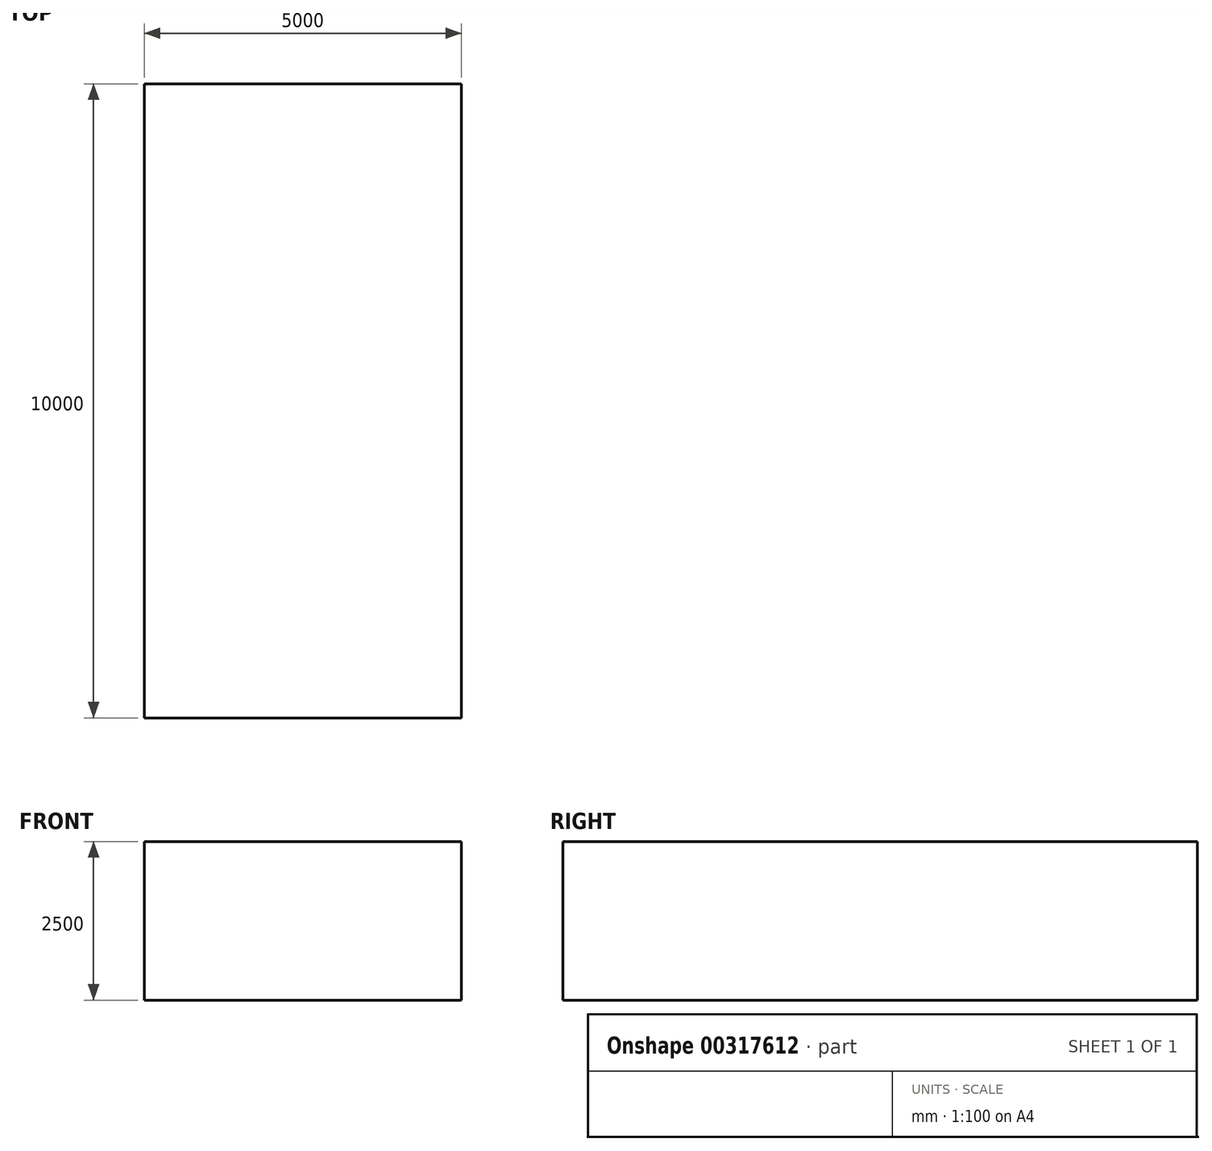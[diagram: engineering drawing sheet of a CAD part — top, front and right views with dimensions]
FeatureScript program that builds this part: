
annotation { "Feature Type Name" : "Feature", "Feature Type Description" : "" }
export const myFeature = defineFeature(function(context is Context, id is Id, definition is map)
    precondition{}
    {
        {
            var Q0;
            Q0=qCreatedBy(makeId("Front.planeOp"),FACE);
            var sketch = newSketch(context, id + "F0", { "sketchPlane" : qUnion([Q0])});
            skLineSegment(sketch, "E0.bottom", {"start": v(-2348.79, 1512.9) * mm, "end": v(2651.21, 1512.9) * mm});
            skLineSegment(sketch, "E0.top", {"start": v(-2348.79, -987.1) * mm, "end": v(2651.21, -987.1) * mm});
            skLineSegment(sketch, "E0.left", {"start": v(-2348.79, 1512.9) * mm, "end": v(-2348.79, -987.1) * mm});
            skLineSegment(sketch, "E0.right", {"start": v(2651.21, 1512.9) * mm, "end": v(2651.21, -987.1) * mm});
            skSolve(sketch);
        }
        {
            var Q0;
            Q0 = qSketchRegion(id + "F0", true);
            extrude(context, id + "F1", {"entities" : qUnion([Q0]), "depth" : 10000 * mm});
        }
    });
